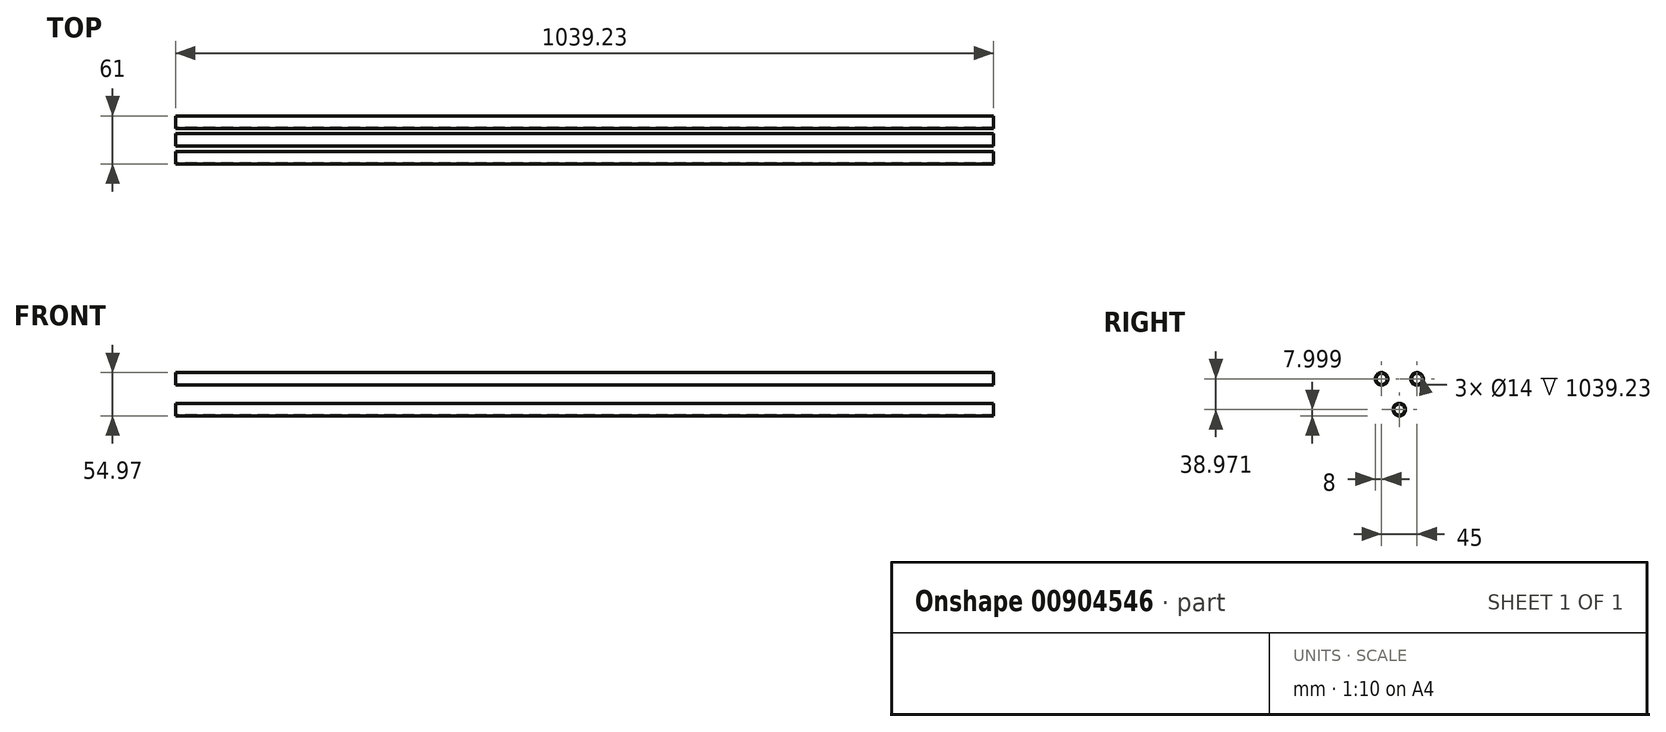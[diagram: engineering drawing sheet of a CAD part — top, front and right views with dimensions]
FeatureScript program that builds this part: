
annotation { "Feature Type Name" : "Feature", "Feature Type Description" : "" }
export const myFeature = defineFeature(function(context is Context, id is Id, definition is map)
    precondition{}
    {
        {
            var Q0;
            Q0=qCreatedBy(makeId("Right.planeOp"),FACE);
            var sketch = newSketch(context, id + "F0", { "sketchPlane" : qUnion([Q0])});
            skCircle(sketch, "E0", {"center": v(0, 0) * mm, "radius": 8 * mm});
            skCircle(sketch, "E1", {"center": v(45, 0) * mm, "radius": 8 * mm});
            skCircle(sketch, "E2", {"center": v(22.5, -38.97) * mm, "radius": 8 * mm});
            skCircle(sketch, "E3", {"center": v(0, 0) * mm, "radius": 7 * mm});
            skCircle(sketch, "E4", {"center": v(45, 0) * mm, "radius": 7 * mm});
            skCircle(sketch, "E5", {"center": v(22.5, -38.97) * mm, "radius": 7 * mm});
            skSolve(sketch);
        }
        {
            var Q0;
            Q0=makeQuery(id+"F0.imprint","IMPRINT",FACE,{"disambiguationData":[TD([[makeQuery(id+"F0.imprint","IMPRINT",EDGE,{"derivedFrom":sQuery(id+"F0.wireOp",EDGE,"E0")}),1.0]])]});
            var Q1;
            Q1=makeQuery(id+"F0.imprint","IMPRINT",FACE,{"disambiguationData":[TD([[makeQuery(id+"F0.imprint","IMPRINT",EDGE,{"derivedFrom":sQuery(id+"F0.wireOp",EDGE,"E1")}),1.0]])]});
            var Q2;
            Q2=makeQuery(id+"F0.imprint","IMPRINT",FACE,{"disambiguationData":[TD([[makeQuery(id+"F0.imprint","IMPRINT",EDGE,{"derivedFrom":sQuery(id+"F0.wireOp",EDGE,"E2")}),1.0]])]});
            extrude(context, id + "F1", {"entities" : qUnion([Q0, Q1, Q2]), "depth" : 1039.23 * mm, "offsetDistance" : 25 * mm});
        }
    });
